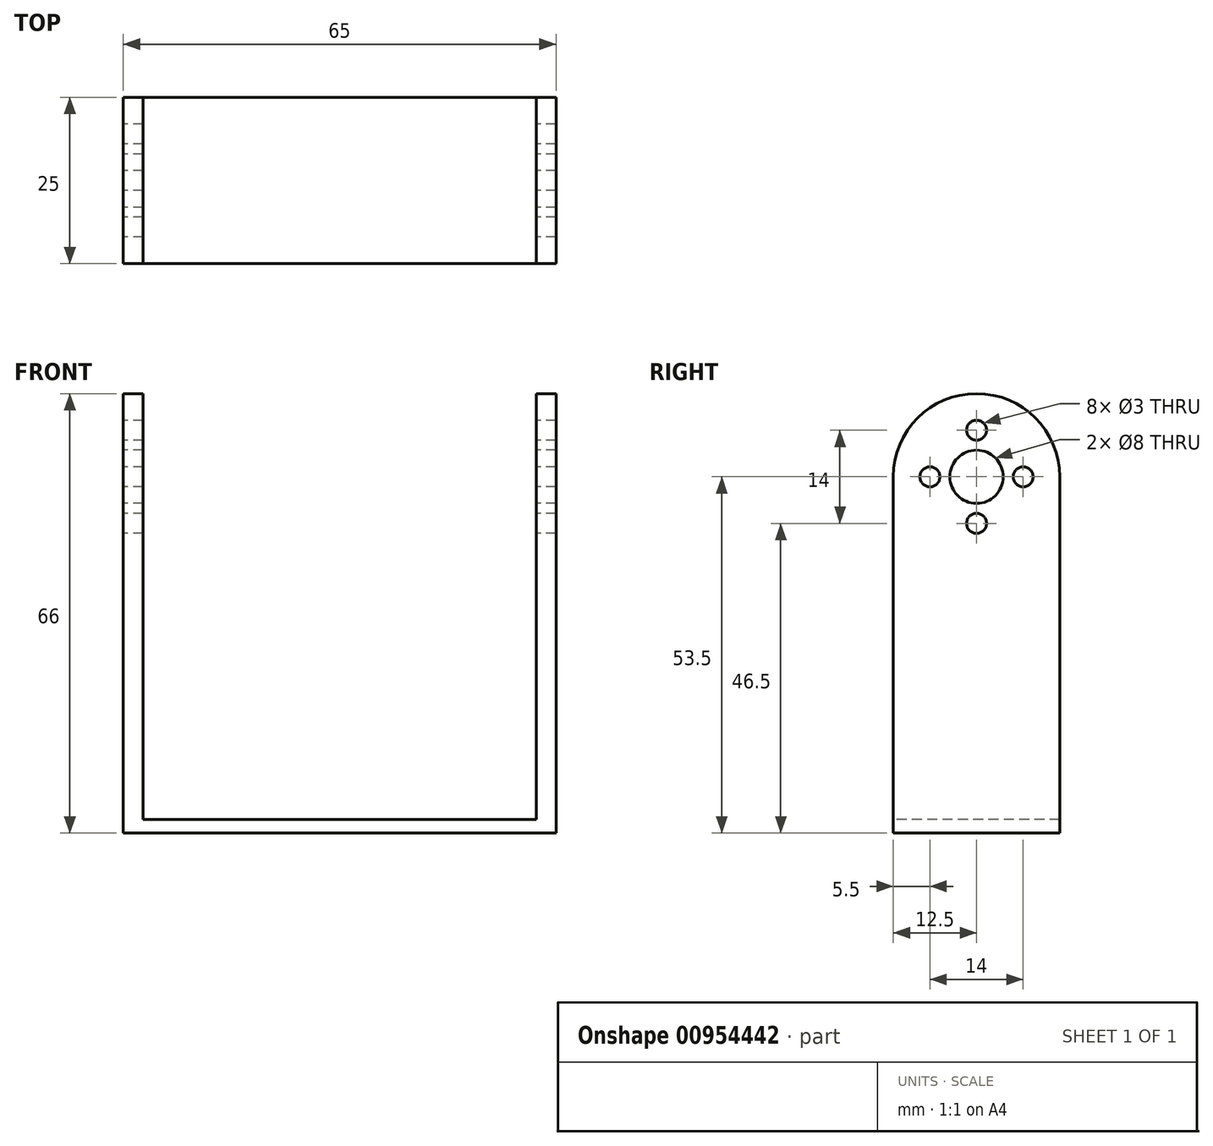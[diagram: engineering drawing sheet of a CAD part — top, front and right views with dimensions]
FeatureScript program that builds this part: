
annotation { "Feature Type Name" : "Feature", "Feature Type Description" : "" }
export const myFeature = defineFeature(function(context is Context, id is Id, definition is map)
    precondition{}
    {
        {
            var Q0;
            Q0=qCreatedBy(makeId("Top.planeOp"),FACE);
            var sketch = newSketch(context, id + "F0", { "sketchPlane" : qUnion([Q0])});
            skLineSegment(sketch, "E0.bottom", {"start": v(0, 0) * mm, "end": v(65, 0) * mm});
            skLineSegment(sketch, "E0.top", {"start": v(0, 25) * mm, "end": v(65, 25) * mm});
            skLineSegment(sketch, "E0.left", {"start": v(0, 0) * mm, "end": v(0, 25) * mm});
            skLineSegment(sketch, "E0.right", {"start": v(65, 0) * mm, "end": v(65, 25) * mm});
            skPoint(sketch, "E1.centerSnap0", {"position": v(0, 12.5) * mm});
            skPoint(sketch, "E1.centerSnap1", {"position": v(32.5, 0) * mm});
            skSolve(sketch);
        }
        {
            var Q0;
            Q0=qSketchRegion(id+"F0",true);
            extrude(context, id + "F1", {"entities" : qUnion([Q0]), "depth" : 2 * mm, "offsetDistance" : 25 * mm});
        }
        {
            var Q0;
            Q0=qCreatedBy(makeId("Top.planeOp"),FACE);
            var sketch = newSketch(context, id + "F2", { "sketchPlane" : qUnion([Q0])});
            skLineSegment(sketch, "E2.bottom", {"start": v(0, 0) * mm, "end": v(3, 0) * mm});
            skLineSegment(sketch, "E2.top", {"start": v(0, 25) * mm, "end": v(3, 25) * mm});
            skLineSegment(sketch, "E2.left", {"start": v(0, 0) * mm, "end": v(0, 25) * mm});
            skLineSegment(sketch, "E2.right", {"start": v(3, 0) * mm, "end": v(3, 25) * mm});
            skLineSegment(sketch, "E3.bottom", {"start": v(62, 0) * mm, "end": v(65, 0) * mm});
            skLineSegment(sketch, "E3.top", {"start": v(62, 25) * mm, "end": v(65, 25) * mm});
            skLineSegment(sketch, "E3.left", {"start": v(62, 0) * mm, "end": v(62, 25) * mm});
            skLineSegment(sketch, "E3.right", {"start": v(65, 0) * mm, "end": v(65, 25) * mm});
            skSolve(sketch);
        }
        {
            var Q0;
            Q0=qSketchRegion(id+"F2",true);
            extrude(context, id + "F3", {"entities" : qUnion([Q0]), "operationType" : NewBodyOperationType.ADD, "depth" : 66 * mm, "offsetDistance" : 25 * mm});
        }
        {
            var Q0;
            Q0=makeQuery(id+"F3.boolean.opBoolean","MERGE",FACE,{"derivedFrom":[makeQuery(id+"F1.opExtrude","SWEPT_FACE",FACE,{"disambiguationData":[OSD([sQuery(id+"F0.wireOp",EDGE,"E0.left")])]}),makeQuery(id+"F3.opExtrude","SWEPT_FACE",FACE,{"disambiguationData":[OSD([sQuery(id+"F2.wireOp",EDGE,"E2.left")])]})]});
            var sketch = newSketch(context, id + "F4", { "sketchPlane" : qUnion([Q0])});
            skArc(sketch, "E4", {"start": v(0, 53.5) * mm, "mid": v(-12.5, 66) * mm, "end": v(-25, 53.5) * mm});
            skPoint(sketch, "E4.centerSnap0", {"position": v(-12.5, 66) * mm});
            skLineSegment(sketch, "E5", {"start": v(-25, 53.5) * mm, "end": v(-25, 66) * mm});
            skLineSegment(sketch, "E6", {"start": v(-25, 66) * mm, "end": v(0, 66) * mm});
            skLineSegment(sketch, "E7", {"start": v(0, 66) * mm, "end": v(0, 53.5) * mm});
            skCircle(sketch, "E8", {"center": v(-12.5, 53.5) * mm, "radius": 4 * mm});
            skCircle(sketch, "E9", {"center": v(-12.5, 60.5) * mm, "radius": 1.5 * mm});
            skCircle(sketch, "E10.1.0", {"center": v(-19.5, 53.5) * mm, "radius": 1.5 * mm});
            skCircle(sketch, "E10.2.0", {"center": v(-12.5, 46.5) * mm, "radius": 1.5 * mm});
            skCircle(sketch, "E10.3.0", {"center": v(-5.5, 53.5) * mm, "radius": 1.5 * mm});
            skSolve(sketch);
        }
        {
            var Q0;
            Q0=qSketchRegion(id+"F4",true);
            extrude(context, id + "F5", {"entities" : qUnion([Q0]), "operationType" : NewBodyOperationType.REMOVE, "endBound" : BoundingType.THROUGH_ALL, "oppositeDirection" : true, "depth" : 25 * mm, "offsetDistance" : 25 * mm});
        }
    });
